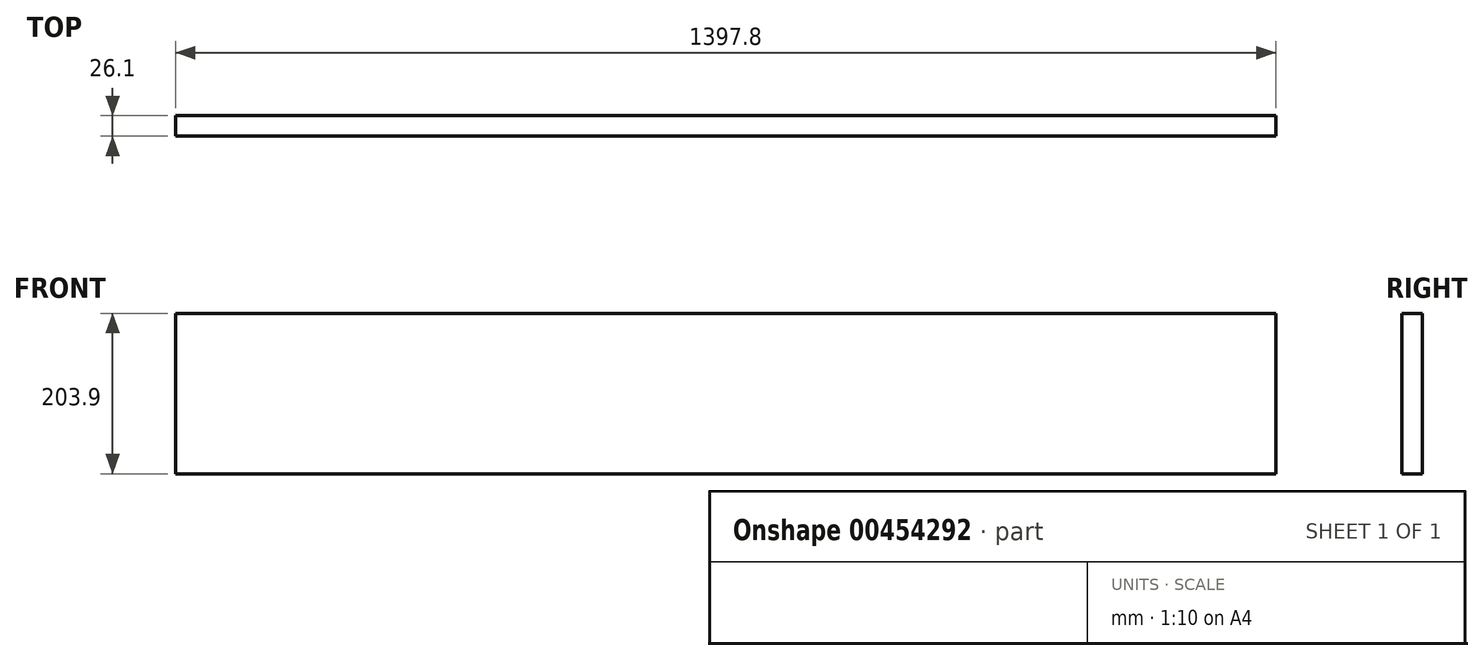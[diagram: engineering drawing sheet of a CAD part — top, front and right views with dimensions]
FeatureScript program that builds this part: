
annotation { "Feature Type Name" : "Feature", "Feature Type Description" : "" }
export const myFeature = defineFeature(function(context is Context, id is Id, definition is map)
    precondition{}
    {
        {
            var Q0;
            Q0=qCreatedBy(makeId("Front.planeOp"),FACE);
            var sketch = newSketch(context, id + "F0", { "sketchPlane" : qUnion([Q0])});
            skLineSegment(sketch, "E0.bottom", {"start": v(698.9, -101.95) * mm, "end": v(-698.9, -101.95) * mm});
            skLineSegment(sketch, "E0.top", {"start": v(698.9, 101.95) * mm, "end": v(-698.9, 101.95) * mm});
            skLineSegment(sketch, "E0.left", {"start": v(698.9, -101.95) * mm, "end": v(698.9, 101.95) * mm});
            skLineSegment(sketch, "E0.right", {"start": v(-698.9, -101.95) * mm, "end": v(-698.9, 101.95) * mm});
            skPoint(sketch, "E0.middle", {"position": v(0, 0) * mm});
            skSolve(sketch);
        }
        {
            var Q0;
            Q0 = qSketchRegion(id + "F0", true);
            extrude(context, id + "F1", {"entities" : qUnion([Q0]), "depth" : 26.1 * mm});
        }
    });
